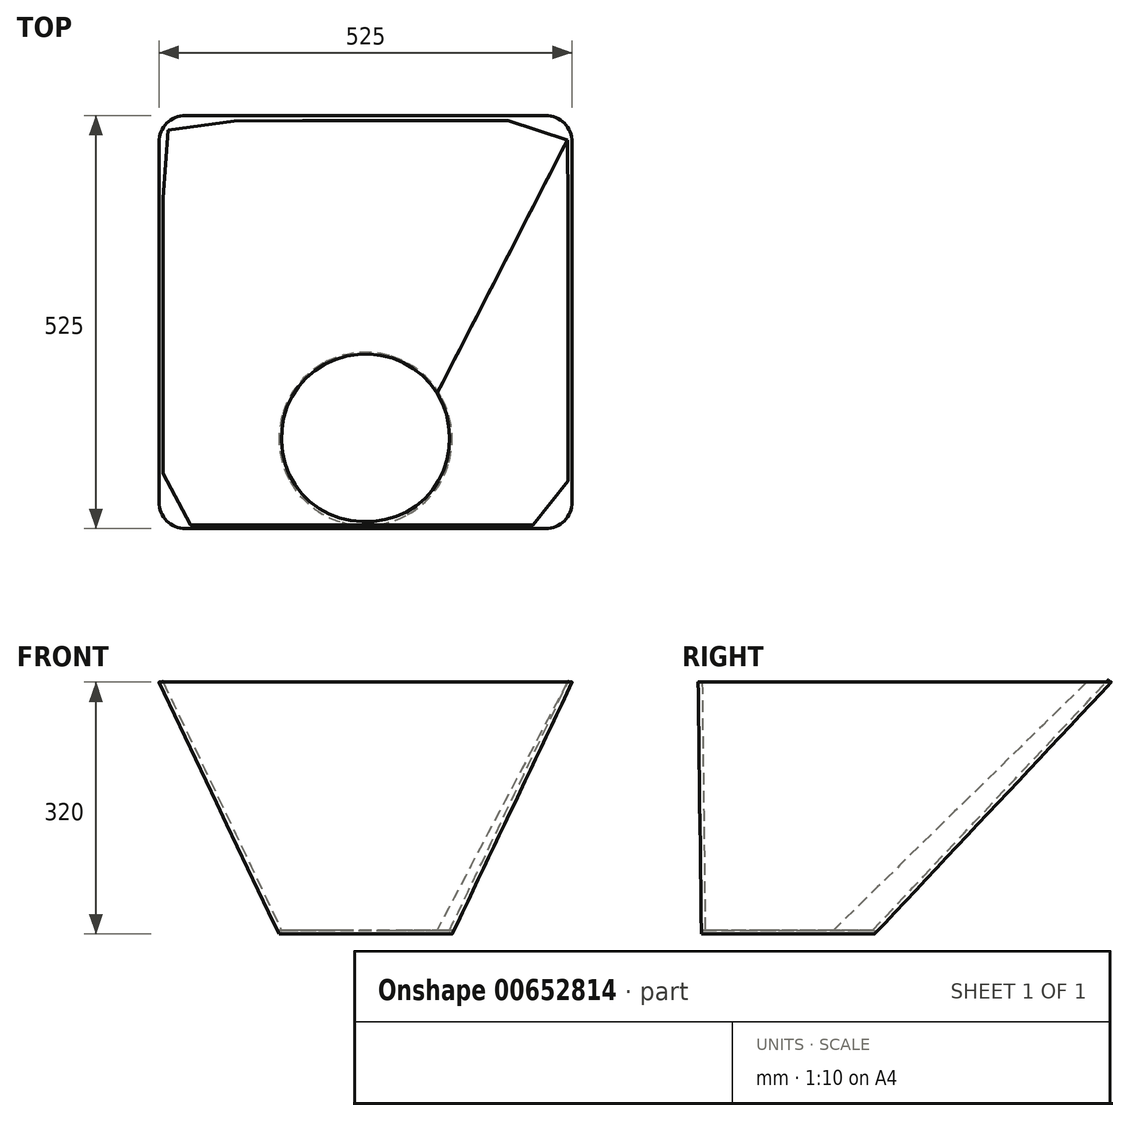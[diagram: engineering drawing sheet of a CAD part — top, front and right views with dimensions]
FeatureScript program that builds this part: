
annotation { "Feature Type Name" : "Feature", "Feature Type Description" : "" }
export const myFeature = defineFeature(function(context is Context, id is Id, definition is map)
    precondition{}
    {
        {
            var Q0;
            Q0=qCreatedBy(makeId("Top.planeOp"),FACE);
            var sketch = newSketch(context, id + "F0", { "sketchPlane" : qUnion([Q0])});
            skCircle(sketch, "E0", {"center": v(0, 0) * mm, "radius": 75 * mm, "construction": true});
            skLineSegment(sketch, "E1", {"start": v(-108.28, 75) * mm, "end": v(138.97, 75) * mm, "construction": true});
            skCircle(sketch, "E2", {"center": v(0, -85) * mm, "radius": 160 * mm});
            skSolve(sketch);
        }
        {
            var Q0;
            Q0=makeQuery(id+"F0.imprint","IMPRINT",FACE,{"disambiguationData":[TD([[makeQuery(id+"F0.imprint","IMPRINT",EDGE,{"derivedFrom":sQuery(id+"F0.wireOp",EDGE,"E2")}),1.0]])]});
            cPlane(context, id + "F1", {"entities" : qUnion([Q0]), "cplaneType" : CPlaneType.OFFSET, "offset" : 520 * mm, "width" : 150 * mm, "height" : 150 * mm});
        }
        {
            var Q0;
            Q0=qCreatedBy(id+"F1.planeOp",FACE);
            var sketch = newSketch(context, id + "F2", { "sketchPlane" : qUnion([Q0])});
            skLineSegment(sketch, "E3.bottom", {"start": v(-228.5, 320) * mm, "end": v(228.5, 320) * mm});
            skLineSegment(sketch, "E3.top", {"start": v(-228.5, -205) * mm, "end": v(228.5, -205) * mm});
            skLineSegment(sketch, "E3.left", {"start": v(-262.5, 286) * mm, "end": v(-262.5, -171) * mm});
            skLineSegment(sketch, "E3.right", {"start": v(262.5, 286) * mm, "end": v(262.5, -171) * mm});
            skPoint(sketch, "E4.visualSharp", {"position": v(-262.5, 320) * mm});
            skArc(sketch, "E4.filletArc", {"start": v(-228.5, 320) * mm, "mid": v(-252.54, 310.04) * mm, "end": v(-262.5, 286) * mm});
            skPoint(sketch, "E5.visualSharp", {"position": v(262.5, 320) * mm});
            skArc(sketch, "E5.filletArc", {"start": v(262.5, 286) * mm, "mid": v(252.54, 310.04) * mm, "end": v(228.5, 320) * mm});
            skPoint(sketch, "E6.visualSharp", {"position": v(262.5, -205) * mm});
            skArc(sketch, "E6.filletArc", {"start": v(228.5, -205) * mm, "mid": v(252.54, -195.04) * mm, "end": v(262.5, -171) * mm});
            skPoint(sketch, "E7.visualSharp", {"position": v(-262.5, -205) * mm});
            skArc(sketch, "E7.filletArc", {"start": v(-262.5, -171) * mm, "mid": v(-252.54, -195.04) * mm, "end": v(-228.5, -205) * mm});
            skLineSegment(sketch, "E8", {"start": v(-115.1, -75) * mm, "end": v(133.25, -75) * mm, "construction": true});
            skSolve(sketch);
        }
        {
            var Q0;
            Q0=makeQuery(id+"F0.imprint","IMPRINT",FACE,{"disambiguationData":[TD([[makeQuery(id+"F0.imprint","IMPRINT",EDGE,{"derivedFrom":sQuery(id+"F0.wireOp",EDGE,"E2")}),1.0]])]});
            cPlane(context, id + "F3", {"entities" : qUnion([Q0]), "cplaneType" : CPlaneType.OFFSET, "offset" : 200 * mm, "width" : 150 * mm, "height" : 150 * mm});
        }
        {
            var Q0;
            Q0=qCreatedBy(id+"F3.planeOp",FACE);
            var sketch = newSketch(context, id + "F4", { "sketchPlane" : qUnion([Q0])});
            skCircle(sketch, "E9", {"center": v(0, -91) * mm, "radius": 110 * mm});
            skCircle(sketch, "E10.0", {"center": v(0, -85) * mm, "radius": 160 * mm, "construction": true});
            skLineSegment(sketch, "E11.0", {"start": v(-228.5, -205) * mm, "end": v(228.5, -205) * mm});
            skLineSegment(sketch, "E12", {"start": v(0, 0) * mm, "end": v(0, -260.6) * mm, "construction": true});
            skSolve(sketch);
        }
        {
            var Q0;
            Q0=makeQuery(id+"F2.imprint","IMPRINT",FACE,{"disambiguationData":[TD([[makeQuery(id+"F2.imprint","IMPRINT",EDGE,{"derivedFrom":sQuery(id+"F2.wireOp",EDGE,"E3.bottom")}),-1.0]])]});
            var Q1;
            Q1=makeQuery(id+"F4.imprint","IMPRINT",FACE,{"disambiguationData":[TD([[makeQuery(id+"F4.imprint","IMPRINT",EDGE,{"derivedFrom":sQuery(id+"F4.wireOp",EDGE,"E9")}),1.0]])]});
            loft(context, id + "F5", {"sheetProfilesArray" : [{ "sheetProfileEntities" : qUnion([Q0]) }, { "sheetProfileEntities" : qUnion([Q1]) }]});
        }
        {
            var Q0;
            Q0=makeQuery(id+"F5.opLoft","CAP_FACE",FACE,{"disambiguationData":[OSD([makeQuery(id+"F2.imprint","IMPRINT",FACE,{"disambiguationData":[TD([[makeQuery(id+"F2.imprint","IMPRINT",EDGE,{"derivedFrom":sQuery(id+"F2.wireOp",EDGE,"E3.bottom")}),-1.0]])]})])],"isStart":true});
            shell(context, id + "F6", {"entities" : qUnion([Q0]), "thickness" : 5 * mm});
        }
        {
            var Q0;
            Q0=makeQuery(id+"F5.opLoft","CAP_FACE",FACE,{"disambiguationData":[OSD([makeQuery(id+"F4.imprint","IMPRINT",FACE,{"disambiguationData":[TD([[makeQuery(id+"F4.imprint","IMPRINT",EDGE,{"derivedFrom":sQuery(id+"F4.wireOp",EDGE,"E9")}),1.0]])]})])],"isStart":true});
            var sketch = newSketch(context, id + "F7", { "sketchPlane" : qUnion([Q0])});
            skCircle(sketch, "E13", {"center": v(0, 91) * mm, "radius": 110 * mm});
            skLineSegment(sketch, "E14.0", {"start": v(-228.5, 205) * mm, "end": v(228.5, 205) * mm});
            skSolve(sketch);
        }
        {
            var Q0;
            Q0=makeQuery(id+"F7.imprint","IMPRINT",FACE,{"disambiguationData":[TD([[makeQuery(id+"F7.imprint","IMPRINT",EDGE,{"derivedFrom":sQuery(id+"F7.wireOp",EDGE,"E13")}),1.0]])]});
            extrude(context, id + "F8", {"entities" : qUnion([Q0]), "operationType" : NewBodyOperationType.REMOVE, "oppositeDirection" : true, "depth" : 5 * mm, "offsetDistance" : 25 * mm});
        }
    });
